# Revit family: Высоконапорный канальный блок VRF-системы
name_source: partatom
category: Mechanical Equipment
revit_build: Autodesk Revit 2016 (Build: 20150506_1715(x64)
units: mm (PartAtom-declared; Revit-internal decimal feet)

## family parameters
Cut with Voids When Loaded = No
Host = Face
Part Type = Normal
Room Calculation Point = No
Round Connector Dimension = Use Diameter
Shared = No

## types (2) — shared parameters
Default Elevation = 1219.2 mm  [stored 4 ft]
Высота = 470 mm  [stored 1.54199 ft]
Высота воздуховода = 276 mm  [stored 0.905512 ft]
Глубина = 1120 mm  [stored 3.67454 ft]
Диаметр жидкостной трубы = 9.53 mm
Наименование = Высоконапорный канальный блок VRF-системы
Производитель = Electrolux
Таблица модель = Модель
Таблица наименование = Наименование
Таблица параметров = Таблица параметров
Таблица расход воздуха = Расход воздуха
Таблица уровень звукового давления = Уровень звукового давления
Таблица электропитание = Электропитание
Фаза = 1
Частота сети = 50 Hz
Эл. питание(коннектор) = 380 V
Электропитание, (В) = 380

## per-type parameters (varying)
| type | Артикул | Вес | Диаметр газовой трубы | Расход воздуха, (м.куб/ч) | Теплопроизводительность | Уровень звукового давления, (Дб(А)) | Холодопроизводительность | Ширина | Ширина воздуховода |
| ESVMD-SF-224-A | 1022707 | 94.00 kg | 19.05 mm  [stored 0.0625 ft] | 3480 | 25.00 kW | 52 | 22.40 kW | 1060 mm  [stored 3.47769 ft] | 800 mm  [stored 2.62467 ft] |
| ESVMD-SF-280-A | 1022708 | 106.00 kg | 22.2 mm  [stored 0.0728346 ft] | 4650 | 31.50 kW | 54 | 28.00 kW | 1250 mm  [stored 4.10105 ft] | 990 mm  [stored 3.24803 ft] |

note: column(s) folded — value = type name in every type: Модель

note: [stored X ft] marks values corroborated as IEEE doubles in the binary element streams (Revit-internal decimal feet)
